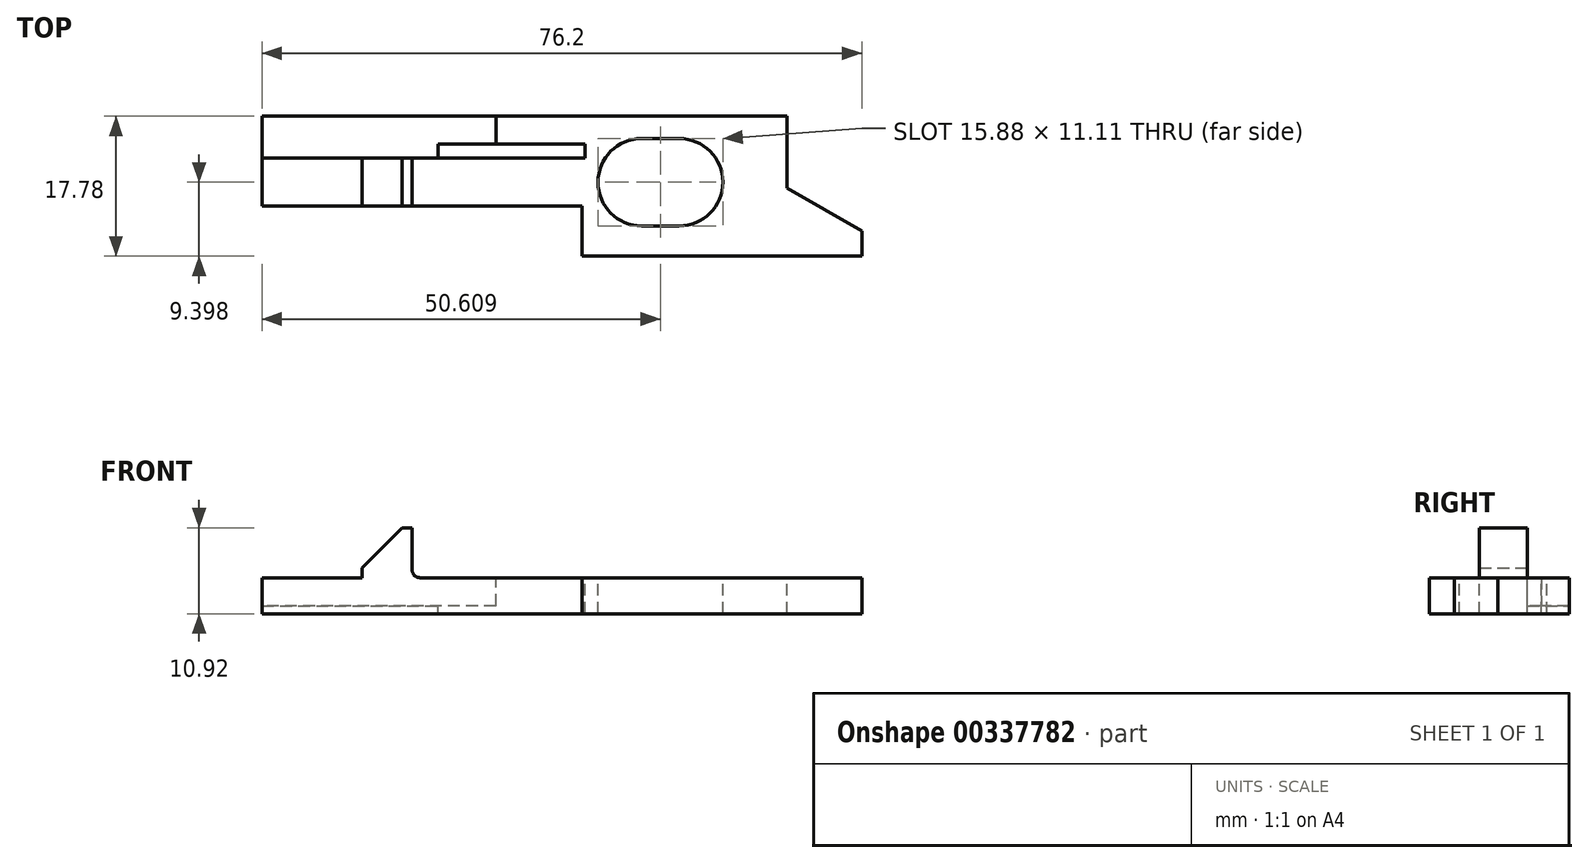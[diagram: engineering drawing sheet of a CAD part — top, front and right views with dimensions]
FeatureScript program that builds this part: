
annotation { "Feature Type Name" : "Feature", "Feature Type Description" : "" }
export const myFeature = defineFeature(function(context is Context, id is Id, definition is map)
    precondition{}
    {
        {
            var Q0;
            Q0=qCreatedBy(makeId("Top.planeOp"),FACE);
            var sketch = newSketch(context, id + "F0", { "sketchPlane" : qUnion([Q0])});
            skLineSegment(sketch, "E0.bottom", {"start": v(38.1, -8.89) * mm, "end": v(-38.1, -8.9) * mm});
            skLineSegment(sketch, "E0.top", {"start": v(38.1, 8.9) * mm, "end": v(-38.1, 8.89) * mm});
            skLineSegment(sketch, "E0.left", {"start": v(38.1, -8.89) * mm, "end": v(38.1, 8.9) * mm});
            skLineSegment(sketch, "E0.right", {"start": v(-38.1, -8.9) * mm, "end": v(-38.1, 8.9) * mm});
            skPoint(sketch, "E0.middle", {"position": v(0, 0) * mm});
            skSolve(sketch);
        }
        {
            var Q0;
            Q0 = qSketchRegion(id + "F0", true);
            extrude(context, id + "F1", {"entities" : qUnion([Q0]), "depth" : 4.57 * mm});
        }
        {
            var Q0;
            Q0=makeQuery(id+"F1.opExtrude","CAP_FACE",FACE,{"disambiguationData":[OSD([sQuery(id+"F0.wireOp",EDGE,"E0.bottom"),sQuery(id+"F0.wireOp",EDGE,"E0.top"),sQuery(id+"F0.wireOp",EDGE,"E0.left"),sQuery(id+"F0.wireOp",EDGE,"E0.right")])],"isStart":false});
            var sketch = newSketch(context, id + "F2", { "sketchPlane" : qUnion([Q0])});
            skLineSegment(sketch, "E1.bottom", {"start": v(-38.1, 8.9) * mm, "end": v(-8.38, 8.9) * mm});
            skLineSegment(sketch, "E1.top", {"start": v(-38.1, 3.56) * mm, "end": v(-8.38, 3.56) * mm});
            skLineSegment(sketch, "E1.left", {"start": v(-38.1, 8.9) * mm, "end": v(-38.1, 3.56) * mm});
            skLineSegment(sketch, "E1.right", {"start": v(-8.38, 8.9) * mm, "end": v(-8.38, 3.56) * mm});
            skSolve(sketch);
        }
        {
            var Q0;
            Q0 = qSketchRegion(id + "F2", true);
            var Q1;
            Q1=makeQuery(id+"F1.opExtrude","CAP_FACE",FACE,{"disambiguationData":[OSD([sQuery(id+"F0.wireOp",EDGE,"E0.bottom"),sQuery(id+"F0.wireOp",EDGE,"E0.top"),sQuery(id+"F0.wireOp",EDGE,"E0.left"),sQuery(id+"F0.wireOp",EDGE,"E0.right")])],"isStart":true});
            extrude(context, id + "F3", {"entities" : qUnion([Q0]), "operationType" : NewBodyOperationType.REMOVE, "oppositeDirection" : true, "endBoundEntityFace" : qUnion([Q1]), "depth" : 3.56 * mm});
        }
        {
            var Q0;
            Q0=makeQuery(id+"F1.opExtrude","CAP_FACE",FACE,{"disambiguationData":[OSD([sQuery(id+"F0.wireOp",EDGE,"E0.bottom"),sQuery(id+"F0.wireOp",EDGE,"E0.top"),sQuery(id+"F0.wireOp",EDGE,"E0.left"),sQuery(id+"F0.wireOp",EDGE,"E0.right")])],"isStart":false});
            var sketch = newSketch(context, id + "F4", { "sketchPlane" : qUnion([Q0])});
            skLineSegment(sketch, "E2.bottom", {"start": v(2.92, 5.37) * mm, "end": v(-15.75, 5.37) * mm});
            skLineSegment(sketch, "E2.top", {"start": v(2.92, 3.56) * mm, "end": v(-15.75, 3.56) * mm});
            skLineSegment(sketch, "E2.left", {"start": v(2.92, 5.37) * mm, "end": v(2.92, 3.56) * mm});
            skLineSegment(sketch, "E2.right", {"start": v(-15.75, 5.37) * mm, "end": v(-15.75, 3.56) * mm});
            skSolve(sketch);
        }
        {
            var Q0;
            Q0 = qSketchRegion(id + "F4", true);
            extrude(context, id + "F5", {"entities" : qUnion([Q0]), "operationType" : NewBodyOperationType.REMOVE, "endBound" : BoundingType.THROUGH_ALL, "oppositeDirection" : true, "depth" : 25.4 * mm});
        }
        {
            var Q0;
            Q0=makeQuery(id+"F1.opExtrude","CAP_FACE",FACE,{"disambiguationData":[OSD([sQuery(id+"F0.wireOp",EDGE,"E0.bottom"),sQuery(id+"F0.wireOp",EDGE,"E0.top"),sQuery(id+"F0.wireOp",EDGE,"E0.left"),sQuery(id+"F0.wireOp",EDGE,"E0.right")])],"isStart":false});
            var sketch = newSketch(context, id + "F6", { "sketchPlane" : qUnion([Q0])});
            skLineSegment(sketch, "E3.bottom", {"start": v(-38.1, -8.9) * mm, "end": v(2.54, -8.9) * mm});
            skLineSegment(sketch, "E3.top", {"start": v(-38.1, -2.54) * mm, "end": v(2.54, -2.54) * mm});
            skLineSegment(sketch, "E3.left", {"start": v(-38.1, -8.9) * mm, "end": v(-38.1, -2.54) * mm});
            skLineSegment(sketch, "E3.right", {"start": v(2.54, -8.9) * mm, "end": v(2.54, -2.54) * mm});
            skSolve(sketch);
        }
        {
            var Q0;
            Q0 = qSketchRegion(id + "F6", true);
            extrude(context, id + "F7", {"entities" : qUnion([Q0]), "operationType" : NewBodyOperationType.REMOVE, "endBound" : BoundingType.THROUGH_ALL, "oppositeDirection" : true, "depth" : 25.4 * mm});
        }
        {
            var Q0;
            Q0=makeQuery(id+"F1.opExtrude","CAP_FACE",FACE,{"disambiguationData":[OSD([sQuery(id+"F0.wireOp",EDGE,"E0.bottom"),sQuery(id+"F0.wireOp",EDGE,"E0.top"),sQuery(id+"F0.wireOp",EDGE,"E0.left"),sQuery(id+"F0.wireOp",EDGE,"E0.right")])],"isStart":false});
            var sketch = newSketch(context, id + "F8", { "sketchPlane" : qUnion([Q0])});
            skArc(sketch, "E4", {"start": v(10.13, 6.06) * mm, "mid": v(4.57, 0.5) * mm, "end": v(10.13, -5.05) * mm});
            skPoint(sketch, "E5.endSnap0", {"position": v(-38.1, 0.5) * mm});
            skLineSegment(sketch, "E6", {"start": v(-38.1, 0.5) * mm, "end": v(4.57, 0.5) * mm, "construction": true});
            skLineSegment(sketch, "E7", {"start": v(10.13, 6.06) * mm, "end": v(14.9, 6.06) * mm});
            skLineSegment(sketch, "E8", {"start": v(10.13, -5.05) * mm, "end": v(14.9, -5.05) * mm});
            skArc(sketch, "E9", {"start": v(14.9, -5.05) * mm, "mid": v(20.45, 0.5) * mm, "end": v(14.9, 6.06) * mm});
            skLineSegment(sketch, "E10", {"start": v(10.13, 0.5) * mm, "end": v(35.53, 0.5) * mm, "construction": true});
            skSolve(sketch);
        }
        {
            var Q0;
            Q0=makeQuery(id+"F8.imprint","IMPRINT",FACE,{"disambiguationData":[TD([[makeQuery(id+"F8.imprint","IMPRINT",EDGE,{"derivedFrom":sQuery(id+"F8.wireOp",EDGE,"E4")}),-1.0]])]});
            var sketch = newSketch(context, id + "F9", { "sketchPlane" : qUnion([Q0])});
            skLineSegment(sketch, "E11", {"start": v(38.1, 8.9) * mm, "end": v(28.58, 8.9) * mm});
            skLineSegment(sketch, "E12", {"start": v(38.1, -5.71) * mm, "end": v(38.1, 8.9) * mm});
            skLineSegment(sketch, "E13", {"start": v(38.1, -5.72) * mm, "end": v(28.58, -0.22) * mm});
            skLineSegment(sketch, "E14", {"start": v(28.58, -0.22) * mm, "end": v(28.58, 8.9) * mm});
            skSolve(sketch);
        }
        {
            var Q0;
            Q0 = qSketchRegion(id + "F9", true);
            extrude(context, id + "F10", {"entities" : qUnion([Q0]), "operationType" : NewBodyOperationType.REMOVE, "oppositeDirection" : true, "depth" : 25.4 * mm});
        }
        {
            var Q0;
            Q0 = qSketchRegion(id + "F8", true);
            extrude(context, id + "F11", {"entities" : qUnion([Q0]), "operationType" : NewBodyOperationType.REMOVE, "oppositeDirection" : true, "depth" : 25.4 * mm});
        }
        {
            var Q0;
            Q0=makeQuery(id+"F1.opExtrude","CAP_FACE",FACE,{"disambiguationData":[OSD([sQuery(id+"F0.wireOp",EDGE,"E0.bottom"),sQuery(id+"F0.wireOp",EDGE,"E0.top"),sQuery(id+"F0.wireOp",EDGE,"E0.left"),sQuery(id+"F0.wireOp",EDGE,"E0.right")])],"isStart":false});
            var sketch = newSketch(context, id + "F12", { "sketchPlane" : qUnion([Q0])});
            skLineSegment(sketch, "E15.bottom", {"start": v(-25.4, 3.56) * mm, "end": v(-19.05, 3.56) * mm});
            skLineSegment(sketch, "E15.top", {"start": v(-25.4, -2.54) * mm, "end": v(-19.05, -2.54) * mm});
            skLineSegment(sketch, "E15.left", {"start": v(-25.4, 3.56) * mm, "end": v(-25.4, -2.54) * mm});
            skLineSegment(sketch, "E15.right", {"start": v(-19.05, 3.56) * mm, "end": v(-19.05, -2.54) * mm});
            skSolve(sketch);
        }
        {
            var Q0;
            Q0 = qSketchRegion(id + "F12", true);
            extrude(context, id + "F13", {"entities" : qUnion([Q0]), "operationType" : NewBodyOperationType.ADD, "depth" : 6.35 * mm});
        }
        {
            var Q0;
            Q0=makeQuery(id+"F13.opExtrude","CAP_EDGE",EDGE,{"disambiguationData":[OSD([sQuery(id+"F12.wireOp",EDGE,"E15.left")])],"isStart":false});
            chamfer(context, id + "F14", {"entities" : qUnion([Q0]), "width" : 5.08 * mm, "tangentPropagation" : true});
        }
        {
            var Q0;
            Q0=makeQuery(id+"F13.opExtrude","CAP_EDGE",EDGE,{"disambiguationData":[OSD([sQuery(id+"F12.wireOp",EDGE,"E15.right")])],"isStart":true});
            var Q1;
            Q1=makeQuery(id+"F13.opExtrude","CAP_EDGE",EDGE,{"disambiguationData":[OSD([sQuery(id+"F12.wireOp",EDGE,"E15.left")])],"isStart":true});
            fillet(context, id + "F15", {"entities" : qUnion([Q0, Q1]), "radius" : 1 * mm, "tangentPropagation" : true, "allowEdgeOverflow" : false});
        }
    });
